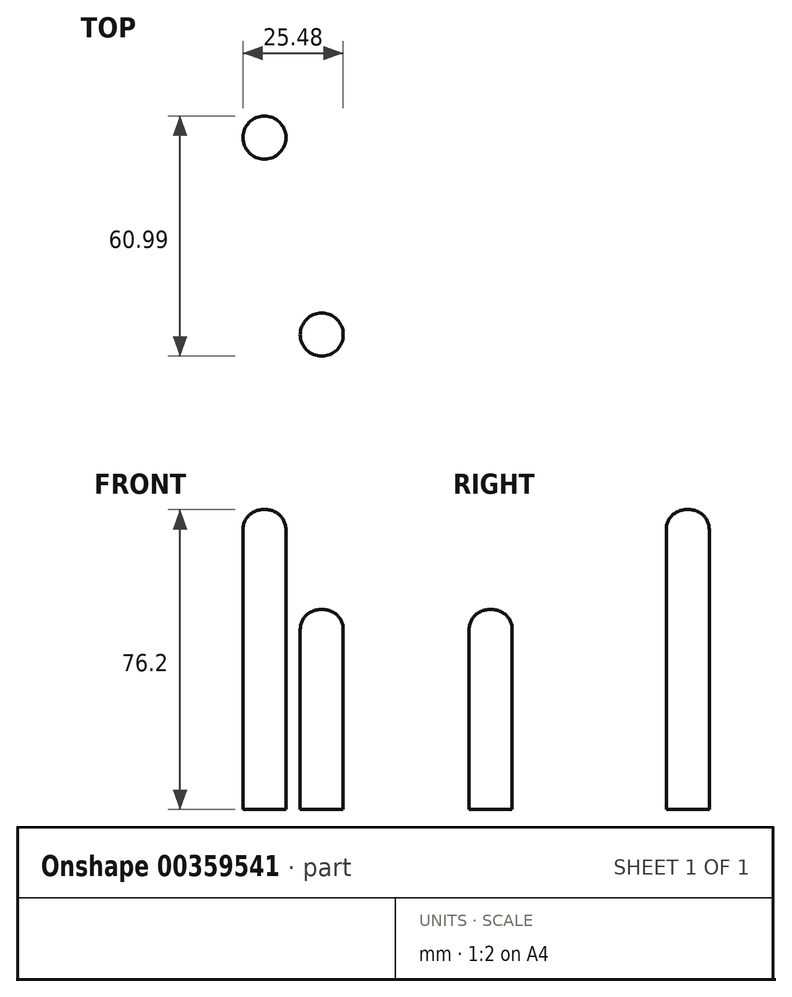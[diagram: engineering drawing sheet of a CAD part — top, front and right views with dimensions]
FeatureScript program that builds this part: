
annotation { "Feature Type Name" : "Feature", "Feature Type Description" : "" }
export const myFeature = defineFeature(function(context is Context, id is Id, definition is map)
    precondition{}
    {
        {
            var Q0;
            Q0=qCreatedBy(makeId("Top.planeOp"),FACE);
            var sketch = newSketch(context, id + "F0", { "sketchPlane" : qUnion([Q0])});
            skCircle(sketch, "E0", {"center": v(-55.78, 17.58) * mm, "radius": 5.46 * mm});
            skSolve(sketch);
        }
        {
            var Q0;
            Q0=makeQuery(id+"F0.imprint","IMPRINT",FACE,{"disambiguationData":[TD([[makeQuery(id+"F0.imprint","IMPRINT",EDGE,{"derivedFrom":sQuery(id+"F0.wireOp",EDGE,"E0")}),1.0]])]});
            extrude(context, id + "F1", {"entities" : qUnion([Q0]), "depth" : 76.2 * mm, "offsetDistance" : 25.4 * mm});
        }
        {
            var Q0;
            Q0=qCreatedBy(makeId("Top.planeOp"),FACE);
            var sketch = newSketch(context, id + "F2", { "sketchPlane" : qUnion([Q0])});
            skCircle(sketch, "E1", {"center": v(-41.22, -32.48) * mm, "radius": 5.46 * mm});
            skSolve(sketch);
        }
        {
            var Q0;
            Q0=makeQuery(id+"F2.imprint","IMPRINT",FACE,{"disambiguationData":[TD([[makeQuery(id+"F2.imprint","IMPRINT",EDGE,{"derivedFrom":sQuery(id+"F2.wireOp",EDGE,"E1")}),1.0]])]});
            extrude(context, id + "F3", {"entities" : qUnion([Q0]), "depth" : 50.8 * mm, "offsetDistance" : 25.4 * mm});
        }
        {
            var Q0;
            Q0=makeQuery(id+"F1.opExtrude","CAP_FACE",FACE,{"disambiguationData":[OSD([sQuery(id+"F0.wireOp",EDGE,"E0")])],"isStart":false});
            var Q1;
            Q1=makeQuery(id+"F3.opExtrude","CAP_FACE",FACE,{"disambiguationData":[OSD([sQuery(id+"F2.wireOp",EDGE,"E1")])],"isStart":false});
            fillet(context, id + "F4", {"entities" : qUnion([Q0, Q1]), "radius" : 5.08 * mm, "tangentPropagation" : true, "allowEdgeOverflow" : false});
        }
    });
